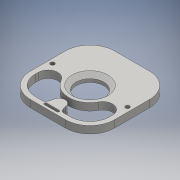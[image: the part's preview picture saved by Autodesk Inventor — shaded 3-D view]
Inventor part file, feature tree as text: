
AUTODESK INVENTOR PART (.ipt)
format: ipt  version: 2016 (Build 200138000, 138)  size: 198,656 bytes
history: native  units: mm
features: extrude x7, sketch x7, fillet x5, chamfer x2, projected_geometry x1
ambient origin geometry x8: Origin, YZ Plane, XZ Plane, XY Plane, X Axis, Y Axis, Z Axis, Center Point
bodies: Solid1 (feature_tree)
feature tree (22):
  extrude  "Extrusion1"  Depth=103.0mm
  extrude  "Extrusion3"  Depth=30.0mm
  fillet  "Fillet1"  Radius=9.0mm
  fillet  "Fillet2"  Radius=30.0mm
  fillet  "Fillet3"  Radius=30.0mm
  extrude  "Extrusion5"  Depth=30.0mm
  extrude  "Extrusion6"  Depth=10.0mm
  chamfer  "Chamfer1"  Distance=10.0mm
  extrude  "Extrusion7"  Depth=6.0mm
  extrude  "Extrusion8"  Depth=24.0mm
  chamfer  "Chamfer2"  Distance=10.0mm
  fillet  "Fillet4"  Radius=20.0mm
  fillet  "Fillet5"  Radius=15.0mm
  extrude  "Extrusion9"  Depth=10.0mm
  sketch  "Sketch1"  dims[d0=103.0mm d1=103.0mm]
  sketch  "Sketch3"  dims[d2=9.0mm d3=0.0mm d7=5.0mm d8=9.0mm d9=0.0mm d10=30.0mm d11=30.0mm]
  sketch  "Sketch7"  dims[d12=30.0mm d17=5.0mm]
  sketch  "Sketch8"  dims[d18=11.0mm d19=0.0mm d20=34.0mm d21=10.0mm d22=0.0mm]
  sketch  "Sketch9"  dims[d23=5.0mm d24=2.0mm d25=45.0deg d26=6.0mm]
  projected_geometry  "Projected Loop1"
  sketch  "Sketch10"  dims[d27=4.0mm d28=24.0mm]
  sketch  "Sketch11"  dims[d29=24.0mm d30=10.0mm d31=0.0mm d32=20.0mm d33=15.0mm d34=15.0mm d35=10.0mm d36=0.0mm d37=5.0mm d38=2.0mm d39=0.872665mm d40=4.0mm d41=4.0mm d42=3.0mm d43=10.0mm d44=0.0mm]
